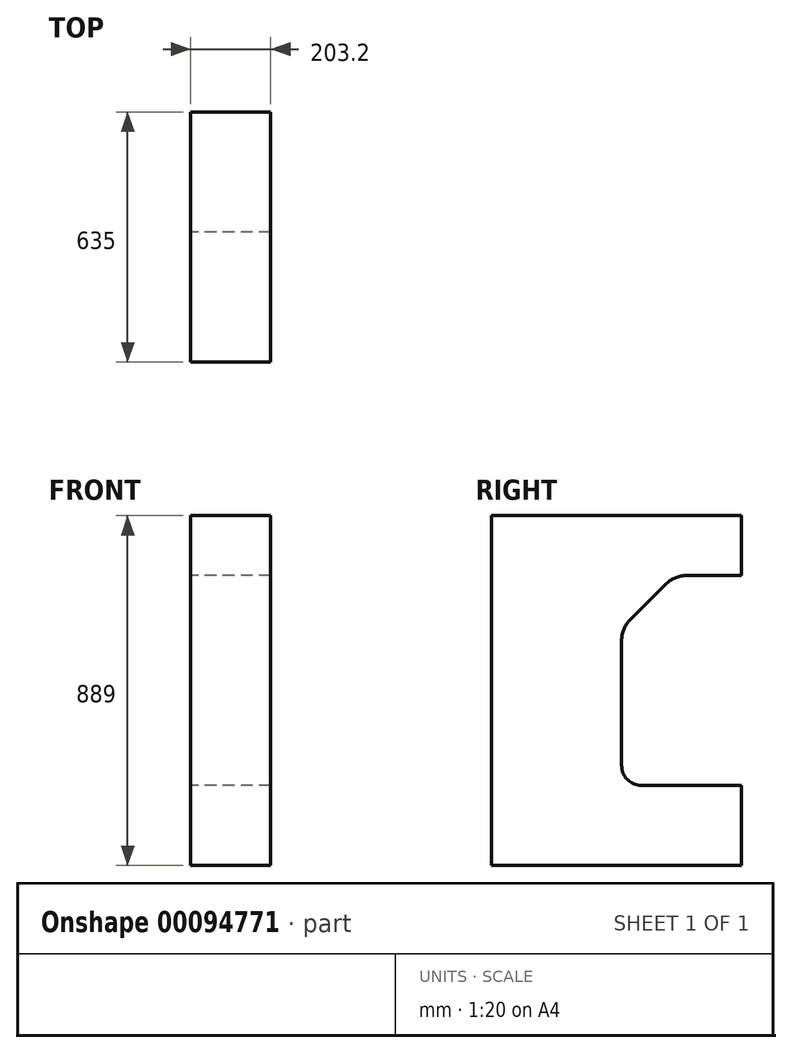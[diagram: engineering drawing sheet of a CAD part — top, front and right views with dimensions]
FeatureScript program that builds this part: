
annotation { "Feature Type Name" : "Feature", "Feature Type Description" : "" }
export const myFeature = defineFeature(function(context is Context, id is Id, definition is map)
    precondition{}
    {
        {
            var Q0;
            Q0=qCreatedBy(makeId("Right.planeOp"),FACE);
            var sketch = newSketch(context, id + "F0", { "sketchPlane" : qUnion([Q0])});
            skLineSegment(sketch, "E0.bottom", {"start": v(-317.5, 444.5) * mm, "end": v(317.5, 444.5) * mm});
            skLineSegment(sketch, "E0.top", {"start": v(-317.5, -444.5) * mm, "end": v(317.5, -444.5) * mm});
            skLineSegment(sketch, "E0.left", {"start": v(-317.5, 444.5) * mm, "end": v(-317.5, -444.5) * mm});
            skLineSegment(sketch, "E0.right", {"start": v(317.5, 444.5) * mm, "end": v(317.5, 292.1) * mm});
            skPoint(sketch, "E0.middle", {"position": v(0, 0) * mm});
            skLineSegment(sketch, "E1", {"start": v(317.5, -241.3) * mm, "end": v(63.5, -241.3) * mm});
            skLineSegment(sketch, "E2", {"start": v(12.7, -190.5) * mm, "end": v(12.7, 126.56) * mm});
            skLineSegment(sketch, "E3", {"start": v(35.02, 180.44) * mm, "end": v(124.36, 269.78) * mm});
            skLineSegment(sketch, "E4", {"start": v(178.24, 292.1) * mm, "end": v(317.5, 292.1) * mm});
            skPoint(sketch, "E5.visualSharp", {"position": v(146.67, 292.1) * mm});
            skArc(sketch, "E5.filletArc", {"start": v(178.24, 292.1) * mm, "mid": v(149.08, 286.3) * mm, "end": v(124.36, 269.78) * mm});
            skPoint(sketch, "E6.visualSharp", {"position": v(12.7, 158.13) * mm});
            skArc(sketch, "E6.filletArc", {"start": v(35.02, 180.44) * mm, "mid": v(18.5, 155.72) * mm, "end": v(12.7, 126.56) * mm});
            skPoint(sketch, "E7.visualSharp", {"position": v(12.7, -241.3) * mm});
            skArc(sketch, "E7.filletArc", {"start": v(12.7, -190.5) * mm, "mid": v(27.58, -226.42) * mm, "end": v(63.5, -241.3) * mm});
            skLineSegment(sketch, "E8.trimOffspring", {"start": v(317.5, -241.3) * mm, "end": v(317.5, -444.5) * mm});
            skSolve(sketch);
        }
        {
            var Q0;
            Q0 = qSketchRegion(id + "F0", true);
            extrude(context, id + "F1", {"entities" : qUnion([Q0]), "endBound" : BoundingType.SYMMETRIC, "depth" : 203.2 * mm});
        }
    });
